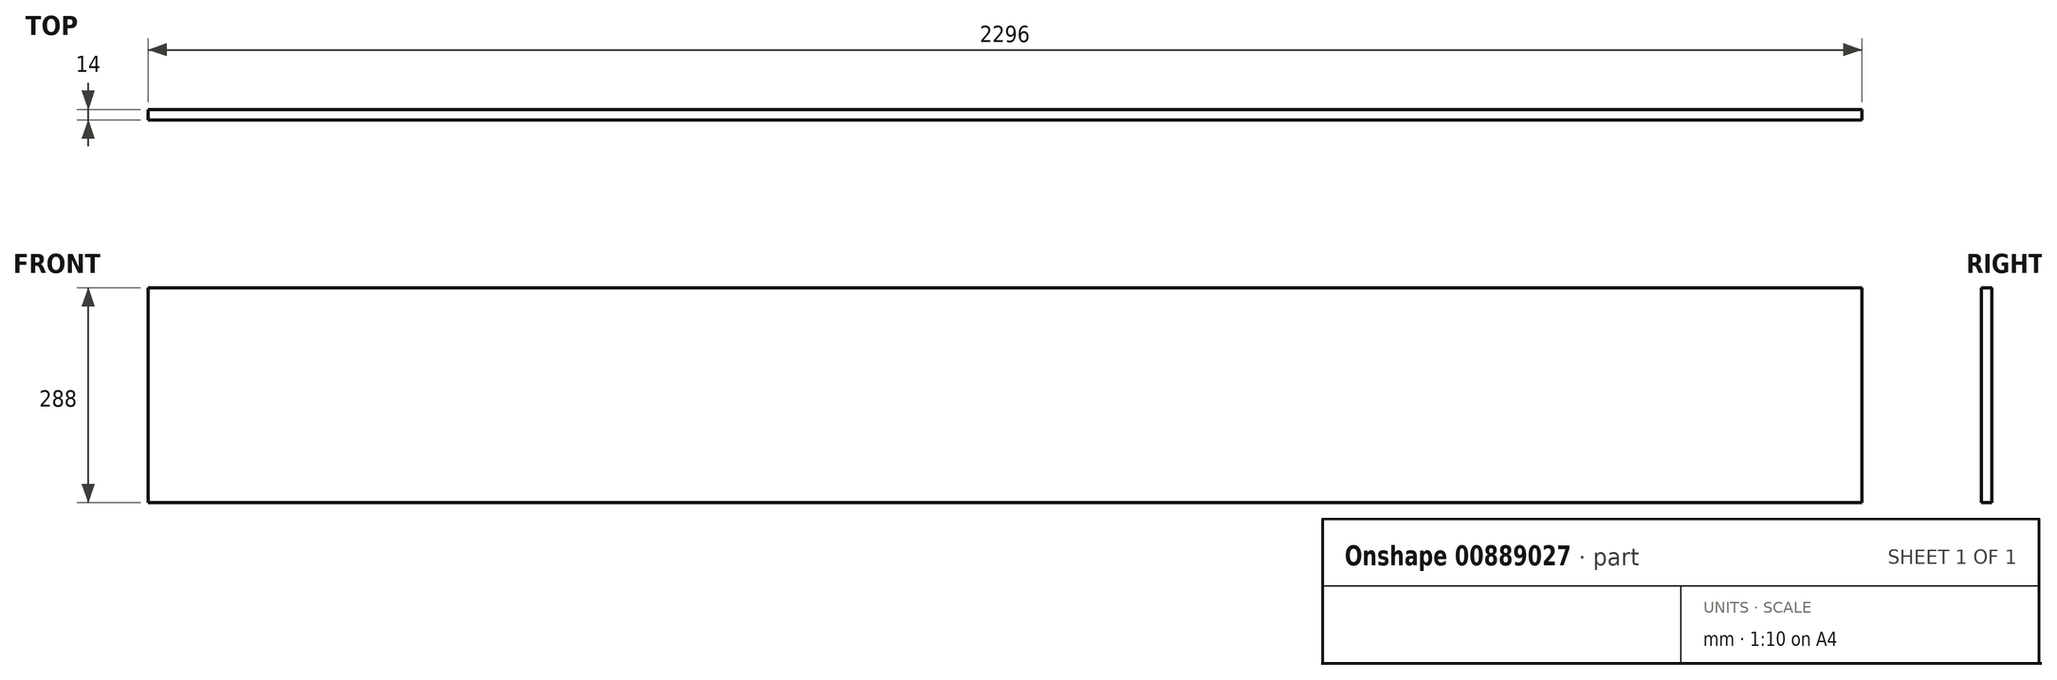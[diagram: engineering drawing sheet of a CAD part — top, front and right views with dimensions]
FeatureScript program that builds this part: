
annotation { "Feature Type Name" : "Feature", "Feature Type Description" : "" }
export const myFeature = defineFeature(function(context is Context, id is Id, definition is map)
    precondition{}
    {
        {
            var Q0;
            Q0=qCreatedBy(makeId("Right.planeOp"),FACE);
            var sketch = newSketch(context, id + "F0", { "sketchPlane" : qUnion([Q0])});
            skLineSegment(sketch, "E0.bottom", {"start": v(-7, 144) * mm, "end": v(7, 144) * mm});
            skLineSegment(sketch, "E0.top", {"start": v(-7, -144) * mm, "end": v(7, -144) * mm});
            skLineSegment(sketch, "E0.left", {"start": v(-7, 144) * mm, "end": v(-7, -144) * mm});
            skLineSegment(sketch, "E0.right", {"start": v(7, 144) * mm, "end": v(7, -144) * mm});
            skPoint(sketch, "E0.middle", {"position": v(0, 0) * mm});
            skSolve(sketch);
        }
        {
            var Q0;
            Q0=qSketchRegion(id+"F0",true);
            extrude(context, id + "F1", {"entities" : qUnion([Q0]), "endBound" : BoundingType.SYMMETRIC, "depth" : (3650 - 1381 + 27) * mm, "offsetDistance" : 25 * mm});
        }
    });
